MODEL slx_faca82ad9bd2
CONFIG AbsTol = auto
CONFIG EnableMultiTasking = off
CONFIG FixedStep = 1e-3
CONFIG MaxStep = auto
CONFIG MinStep = auto
CONFIG RelTol = 1e-3
CONFIG SampleTimeConstraint = Unconstrained
CONFIG Solver = ode14x
CONFIG SolverName = ode14x
CONFIG StartTime = 0.0
CONFIG StopTime = 15
BLOCK [SubSystem] Classical SMC
  Ports = [1]
  RequestExecContextInheritance = off
BLOCK [Gain] Classical SMC/1//M
  Gain = 1/78020
BLOCK [From] Classical SMC/Actual ouput
  GotoTag = Y
BLOCK [Sum] Classical SMC/Add1
  IconShape = rectangular
  Inputs = -+
  Ports = [2, 1]
BLOCK [Sum] Classical SMC/Add2
  IconShape = rectangular
  Inputs = +++-
  Ports = [4, 1]
BLOCK [Derivative] Classical SMC/Derivative
  NameLocation = left
BLOCK [Derivative] Classical SMC/Derivative1
BLOCK [Derivative] Classical SMC/Derivative2
  NameLocation = top
BLOCK [From] Classical SMC/Disturbance Input
  GotoTag = D
BLOCK [From] Classical SMC/Error
  GotoTag = E
BLOCK [Gain] Classical SMC/Force to Voltage
  Gain = 1/ 2871.14
BLOCK [FromWorkspace] Classical SMC/From Workspace2
  OutDataTypeStr = double
  OutputAfterFinalValue = Setting to zero
  VariableName = Cut1500down
BLOCK [Gain] Classical SMC/Gain, K
  Gain = 0.01
BLOCK [Gain] Classical SMC/Gain1
  Gain = 163
BLOCK [Gain] Classical SMC/Gain2
  Gain = 193.3
BLOCK [Goto] Classical SMC/Goto
  GotoTag = C_SMC
  TagVisibility = global
BLOCK [Goto] Classical SMC/Goto1
  GotoTag = R
BLOCK [Goto] Classical SMC/Goto2
  GotoTag = E
BLOCK [Goto] Classical SMC/Goto3
  GotoTag = Y
BLOCK [Goto] Classical SMC/Goto4
  GotoTag = D
BLOCK [ManualSwitch] Classical SMC/Manual Switch
  CurrentSetting = 0
BLOCK [ManualSwitch] Classical SMC/Manual Switch1
  NameLocation = left
BLOCK [Inport] Classical SMC/Ref
BLOCK [Sin] Classical SMC/Ref. Position, Xref (mm)
  Amplitude = 5
  Frequency = 0.5*(2*pi)
  Offset = 1/2000
  Ports = [0, 1]
  SampleTime = 0
BLOCK [From] Classical SMC/Reference Input
  GotoTag = R
BLOCK [Scope] Classical SMC/Scope
  Floating = off
  NumInputPorts = 1
  Ports = [1]
  ScopeSpecificationString = Simulink.scopes.TimeScopeBlockCfg('CurrentConfiguration', extmgr.ConfigurationSet(extmgr.Configuration('Core','General UI',true),extmgr.Configuration('Core','Source UI',true),extmgr.Configuration('Sources','WiredSimulink',true),extmgr.Configuration('Visuals','Time Domain',true,'SerializedDisplays',{struct('MinYLimReal','-6.29812','MaxYLimReal','6.30846','YLabelReal','','MinYLimMag','0.00000','MaxY...<+1379ch>  <repeated x3 — deduplicated>
BLOCK [Scope] Classical SMC/Scope1
  Floating = off
  NumInputPorts = 4
  Ports = [4]
  ScopeSpecificationString = Simulink.scopes.TimeScopeBlockCfg('CurrentConfiguration', extmgr.ConfigurationSet(extmgr.Configuration('Core','General UI',true),extmgr.Configuration('Core','Source UI',true),extmgr.Configuration('Sources','WiredSimulink',true,'DataLoggingVariableName','ScopeData1'),extmgr.Configuration('Visuals','Time Domain',true,'SerializedDisplays',{struct('MinYLimReal','-0.0201','MaxYLimReal','0.01185','YLabe...<+3440ch>
BLOCK [Signum] Classical SMC/Sgn
BLOCK [Sum] Classical SMC/Sum
  Inputs = |-+
  Ports = [2, 1]
BLOCK [Sum] Classical SMC/Sum1
  Inputs = |-+
  Ports = [2, 1]
BLOCK [Sum] Classical SMC/Sum2
  Inputs = |++
  Ports = [2, 1]
BLOCK [Sum] Classical SMC/Sum3
  Inputs = ++|
  Ports = [2, 1]
BLOCK [TransferFcn] Classical SMC/Transfer Fcn1
  Denominator = [1 163 193.3]
  Numerator = [78020]
BLOCK [TransportDelay] Classical SMC/Transport Delay
  DelayTime = 0.0012
  Ports = [1, 1]
BLOCK [Gain] Classical SMC/lamda, λ
  Gain = lamda
BLOCK [Gain] Classical SMC/lamda1, λ
  Gain = lamda
BLOCK [SubSystem] Disturbance
  Ports = [0, 1]
  RequestExecContextInheritance = off
BLOCK [Outport] Disturbance/D(s)
BLOCK [Gain] Disturbance/Force to Voltage1
  Gain = 1/ 2871.14
BLOCK [FromWorkspace] Disturbance/From Workspace2
  OutDataTypeStr = double
  OutputAfterFinalValue = Setting to zero
  VariableName = Cut1500down
BLOCK [From] From
  GotoTag = C_SMC
  TagVisibility = global
BLOCK [From] From1
  GotoTag = S_SMC
  TagVisibility = global
BLOCK [From] From2
  GotoTag = ST_SMC
  TagVisibility = global
BLOCK [Sin] Ref. Position, Xref (mm)
  Amplitude = 5
  Frequency = 0.5*(2*pi)
  Offset = 1/2000
  Ports = [0, 1]
  SampleTime = 0
BLOCK [SubSystem] ST SMC
  Ports = [1]
  RequestExecContextInheritance = off
BLOCK [Gain] ST SMC/1//M
  Gain = 1/78020
BLOCK [Abs] ST SMC/Abs
  SaturateOnIntegerOverflow = off
BLOCK [From] ST SMC/Actual ouput
  GotoTag = Y
BLOCK [Sum] ST SMC/Add1
  IconShape = rectangular
  Inputs = --+
  Ports = [3, 1]
BLOCK [Sum] ST SMC/Add2
  IconShape = rectangular
  Inputs = +++-
  Ports = [4, 1]
BLOCK [Derivative] ST SMC/Derivative
  NameLocation = left
BLOCK [Derivative] ST SMC/Derivative1
BLOCK [Derivative] ST SMC/Derivative2
  NameLocation = top
BLOCK [From] ST SMC/Disturbance Input
  GotoTag = D
BLOCK [DotProduct] ST SMC/Dot Product
  OutDataTypeStr = Inherit: Inherit via internal rule
BLOCK [From] ST SMC/Error
  GotoTag = E
BLOCK [Gain] ST SMC/Force to Voltage
  Gain = 1/ 2871.14
BLOCK [FromWorkspace] ST SMC/From Workspace2
  OutDataTypeStr = double
  OutputAfterFinalValue = Setting to zero
  VariableName = Cut1500down
BLOCK [Gain] ST SMC/Gain, β
  Gain = 0.08
BLOCK [Gain] ST SMC/Gain1
  Gain = 163
BLOCK [Gain] ST SMC/Gain2
  Gain = 193.3
BLOCK [Goto] ST SMC/Goto
  GotoTag = ST_SMC
  TagVisibility = global
BLOCK [Goto] ST SMC/Goto1
  GotoTag = R
BLOCK [Goto] ST SMC/Goto2
  GotoTag = E
BLOCK [Goto] ST SMC/Goto3
  GotoTag = Y
BLOCK [Goto] ST SMC/Goto4
  GotoTag = D
BLOCK [Integrator] ST SMC/Integrator
  Ports = [1, 1]
BLOCK [ManualSwitch] ST SMC/Manual Switch
  CurrentSetting = 0
BLOCK [ManualSwitch] ST SMC/Manual Switch1
  NameLocation = left
BLOCK [Inport] ST SMC/Ref
BLOCK [Sin] ST SMC/Ref. Position, Xref (mm)
  Amplitude = 5
  Frequency = 0.5*(2*pi)
  Offset = 1/2000
  Ports = [0, 1]
  SampleTime = 0
BLOCK [From] ST SMC/Reference Input
  GotoTag = R
BLOCK [Scope] ST SMC/Scope
  Floating = off
  NumInputPorts = 1
  Ports = [1]
BLOCK [Scope] ST SMC/Scope1
  Floating = off
  NumInputPorts = 4
  Ports = [4]
  ScopeSpecificationString = Simulink.scopes.TimeScopeBlockCfg('CurrentConfiguration', extmgr.ConfigurationSet(extmgr.Configuration('Core','General UI',true),extmgr.Configuration('Core','Source UI',true),extmgr.Configuration('Sources','WiredSimulink',true,'DataLoggingVariableName','ScopeData1'),extmgr.Configuration('Visuals','Time Domain',true,'SerializedDisplays',{struct('MinYLimReal','-0.0201','MaxYLimReal','0.01185','YLabe...<+3440ch>
BLOCK [Signum] ST SMC/Sgn
BLOCK [Sqrt] ST SMC/Sqrt
BLOCK [Sum] ST SMC/Sum
  Inputs = |-+
  Ports = [2, 1]
BLOCK [Sum] ST SMC/Sum1
  Inputs = |-+
  Ports = [2, 1]
BLOCK [Sum] ST SMC/Sum2
  Inputs = |++
  Ports = [2, 1]
BLOCK [Sum] ST SMC/Sum3
  Inputs = ++|
  Ports = [2, 1]
BLOCK [TransferFcn] ST SMC/Transfer Fcn
  Denominator = [1 163 193.3]
  Numerator = [78020]
BLOCK [TransportDelay] ST SMC/Transport Delay
  DelayTime = 0.0012
  Ports = [1, 1]
BLOCK [Gain] ST SMC/alpha, α
  Gain = 0.0024
BLOCK [Gain] ST SMC/lamda, λ
  Gain = lamdast
BLOCK [Gain] ST SMC/lamda1, λ
  Gain = lamdast
BLOCK [Scope] Scope
  Floating = off
  NumInputPorts = 3
  Ports = [3]
  ScopeSpecificationString = Simulink.scopes.TimeScopeBlockCfg('CurrentConfiguration', extmgr.ConfigurationSet(extmgr.Configuration('Core','General UI',true),extmgr.Configuration('Core','Source UI',true),extmgr.Configuration('Sources','WiredSimulink',true,'DataLoggingVariableName','SMC_out','DataLogging',true,'DataLoggingSaveFormat','StructureWithTime'),extmgr.Configuration('Visuals','Time Domain',true,'SerializedDisplays',{s...<+1919ch>
BLOCK [SubSystem] Simoid SMC
  Ports = [1]
  RequestExecContextInheritance = off
BLOCK [Gain] Simoid SMC/1//M
  Gain = 1/78020
BLOCK [Abs] Simoid SMC/Abs
  SaturateOnIntegerOverflow = off
BLOCK [From] Simoid SMC/Actual ouput
  GotoTag = Y
BLOCK [Sum] Simoid SMC/Add1
  IconShape = rectangular
  Inputs = -+
  Ports = [2, 1]
BLOCK [Sum] Simoid SMC/Add2
  IconShape = rectangular
  Inputs = +++-
  Ports = [4, 1]
BLOCK [Derivative] Simoid SMC/Derivative
  NameLocation = left
BLOCK [Derivative] Simoid SMC/Derivative1
BLOCK [Derivative] Simoid SMC/Derivative2
  NameLocation = top
BLOCK [From] Simoid SMC/Disturbance Input
  GotoTag = D
BLOCK [DotProduct] Simoid SMC/Dot Product
  OutDataTypeStr = Inherit: Inherit via internal rule
BLOCK [From] Simoid SMC/Error
  GotoTag = E
BLOCK [Math] Simoid SMC/Exp
  Operator = reciprocal
  Ports = [1, 1]
BLOCK [Gain] Simoid SMC/Force to Voltage
  Gain = 1/ 2871.14
BLOCK [FromWorkspace] Simoid SMC/From Workspace2
  OutDataTypeStr = double
  OutputAfterFinalValue = Setting to zero
  VariableName = Cut1500down
BLOCK [Gain] Simoid SMC/Gain, K
  Gain = 0.1
BLOCK [Gain] Simoid SMC/Gain1
  Gain = 163
BLOCK [Gain] Simoid SMC/Gain2
  Gain = 193.3
BLOCK [Goto] Simoid SMC/Goto
  GotoTag = S_SMC
  TagVisibility = global
BLOCK [Goto] Simoid SMC/Goto1
  GotoTag = R
BLOCK [Goto] Simoid SMC/Goto2
  GotoTag = E
BLOCK [Goto] Simoid SMC/Goto3
  GotoTag = Y
BLOCK [Goto] Simoid SMC/Goto4
  GotoTag = D
BLOCK [ManualSwitch] Simoid SMC/Manual Switch
  CurrentSetting = 0
BLOCK [ManualSwitch] Simoid SMC/Manual Switch1
  NameLocation = left
BLOCK [Inport] Simoid SMC/Ref
BLOCK [Sin] Simoid SMC/Ref. Position, Xref (mm)
  Amplitude = 5
  Frequency = 0.5*(2*pi)
  Offset = 1/2000
  Ports = [0, 1]
  SampleTime = 0
BLOCK [From] Simoid SMC/Reference Input
  GotoTag = R
BLOCK [Scope] Simoid SMC/Scope
  Floating = off
  NumInputPorts = 1
  Ports = [1]
BLOCK [Scope] Simoid SMC/Scope1
  Floating = off
  NumInputPorts = 4
  Ports = [4]
  ScopeSpecificationString = Simulink.scopes.TimeScopeBlockCfg('CurrentConfiguration', extmgr.ConfigurationSet(extmgr.Configuration('Core','General UI',true),extmgr.Configuration('Core','Source UI',true),extmgr.Configuration('Sources','WiredSimulink',true,'DataLoggingVariableName','ScopeData1'),extmgr.Configuration('Visuals','Time Domain',true,'SerializedDisplays',{struct('MinYLimReal','-0.01749','MaxYLimReal','0.01015','YLab...<+3442ch>
BLOCK [Sum] Simoid SMC/Sum
  Inputs = |-+
  Ports = [2, 1]
BLOCK [Sum] Simoid SMC/Sum1
  Inputs = |-+
  Ports = [2, 1]
BLOCK [Sum] Simoid SMC/Sum2
  Inputs = |++
  Ports = [2, 1]
BLOCK [Sum] Simoid SMC/Sum3
  Inputs = ++|
  Ports = [2, 1]
BLOCK [Sum] Simoid SMC/Sum4
  Inputs = |++
  Ports = [2, 1]
BLOCK [TransferFcn] Simoid SMC/Transfer Fcn
  Denominator = [1 163 193.3]
  Numerator = [78020]
BLOCK [TransportDelay] Simoid SMC/Transport Delay
  DelayTime = 0.0012
  Ports = [1, 1]
BLOCK [Constant] Simoid SMC/delta
  Value = 20
BLOCK [Gain] Simoid SMC/lamda, λ
  Gain = lamda
BLOCK [Gain] Simoid SMC/lamda1, λ
  Gain = lamda
BLOCK [Terminator] Terminator
LINE Classical SMC/1//M:1 -> Classical SMC/Add1:2
LINE Classical SMC/Actual ouput:1 -> Classical SMC/Scope1:4
LINE Classical SMC/Add1:1 -> Classical SMC/Sum3:2
LINE Classical SMC/Add2:1 -> Classical SMC/1//M:1
LINE Classical SMC/Derivative1:1 -> Classical SMC/Derivative2:1
LINE Classical SMC/Derivative1:1 -> Classical SMC/Sum1:1
LINE Classical SMC/Derivative2:1 -> Classical SMC/Add2:3
LINE Classical SMC/Derivative:1 -> Classical SMC/Gain1:1
LINE Classical SMC/Derivative:1 -> Classical SMC/Sum1:2
LINE Classical SMC/Disturbance Input:1 -> Classical SMC/Scope1:1
LINE Classical SMC/Error:1 -> Classical SMC/Scope1:2
LINE Classical SMC/Force to Voltage:1 -> Classical SMC/Goto4:1
LINE Classical SMC/Force to Voltage:1 -> Classical SMC/Manual Switch1:1
LINE Classical SMC/From Workspace2:1 -> Classical SMC/Force to Voltage:1
LINE Classical SMC/Gain, K:1 -> Classical SMC/Add1:1
LINE Classical SMC/Gain1:1 -> Classical SMC/Add2:1
LINE Classical SMC/Gain2:1 -> Classical SMC/Add2:2
LINE Classical SMC/Manual Switch1:1 -> Classical SMC/Sum3:1
LINE Classical SMC/Manual Switch:1 -> Classical SMC/Derivative1:1
LINE Classical SMC/Manual Switch:1 -> Classical SMC/Goto1:1
LINE Classical SMC/Manual Switch:1 -> Classical SMC/Sum:1
LINE Classical SMC/Ref. Position, Xref (mm):1 -> Classical SMC/Manual Switch:1
LINE Classical SMC/Ref:1 -> Classical SMC/Manual Switch:2
LINE Classical SMC/Reference Input:1 -> Classical SMC/Scope1:3
LINE Classical SMC/Sgn:1 -> Classical SMC/Gain, K:1
LINE Classical SMC/Sum1:1 -> Classical SMC/Sum2:2
LINE Classical SMC/Sum1:1 -> Classical SMC/lamda1, λ:1
LINE Classical SMC/Sum2:1 -> Classical SMC/Sgn:1
LINE Classical SMC/Sum3:1 -> Classical SMC/Transfer Fcn1:1
LINE Classical SMC/Sum:1 -> Classical SMC/Goto2:1
LINE Classical SMC/Sum:1 -> Classical SMC/Goto:1
LINE Classical SMC/Sum:1 -> Classical SMC/lamda, λ:1
LINE Classical SMC/Transfer Fcn1:1 -> Classical SMC/Transport Delay:1
LINE Classical SMC/Transport Delay:1 -> Classical SMC/Derivative:1
LINE Classical SMC/Transport Delay:1 -> Classical SMC/Gain2:1
LINE Classical SMC/Transport Delay:1 -> Classical SMC/Goto3:1
LINE Classical SMC/Transport Delay:1 -> Classical SMC/Scope:1
LINE Classical SMC/Transport Delay:1 -> Classical SMC/Sum:2
LINE Classical SMC/lamda, λ:1 -> Classical SMC/Sum2:1
LINE Classical SMC/lamda1, λ:1 -> Classical SMC/Add2:4
LINE Disturbance/Force to Voltage1:1 -> Disturbance/D(s):1
LINE Disturbance/From Workspace2:1 -> Disturbance/Force to Voltage1:1
LINE Disturbance:1 -> Terminator:1
LINE From1:1 -> Scope:2
LINE From2:1 -> Scope:3
LINE From:1 -> Scope:1
LINE Ref. Position, Xref (mm):1 -> Classical SMC:1
LINE Ref. Position, Xref (mm):1 -> ST SMC:1
LINE Ref. Position, Xref (mm):1 -> Simoid SMC:1
LINE ST SMC/1//M:1 -> ST SMC/Add1:3
LINE ST SMC/Abs:1 -> ST SMC/Sqrt:1
LINE ST SMC/Actual ouput:1 -> ST SMC/Scope1:4
LINE ST SMC/Add1:1 -> ST SMC/Sum3:2
LINE ST SMC/Add2:1 -> ST SMC/1//M:1
LINE ST SMC/Derivative1:1 -> ST SMC/Derivative2:1
LINE ST SMC/Derivative1:1 -> ST SMC/Sum1:1
LINE ST SMC/Derivative2:1 -> ST SMC/Add2:3
LINE ST SMC/Derivative:1 -> ST SMC/Gain1:1
LINE ST SMC/Derivative:1 -> ST SMC/Sum1:2
LINE ST SMC/Disturbance Input:1 -> ST SMC/Scope1:1
LINE ST SMC/Dot Product:1 -> ST SMC/Add1:1
LINE ST SMC/Error:1 -> ST SMC/Scope1:2
LINE ST SMC/Force to Voltage:1 -> ST SMC/Goto4:1
LINE ST SMC/Force to Voltage:1 -> ST SMC/Manual Switch1:1
LINE ST SMC/From Workspace2:1 -> ST SMC/Force to Voltage:1
LINE ST SMC/Gain, β:1 -> ST SMC/Integrator:1
LINE ST SMC/Gain1:1 -> ST SMC/Add2:1
LINE ST SMC/Gain2:1 -> ST SMC/Add2:2
LINE ST SMC/Integrator:1 -> ST SMC/Add1:2
LINE ST SMC/Manual Switch1:1 -> ST SMC/Sum3:1
LINE ST SMC/Manual Switch:1 -> ST SMC/Derivative1:1
LINE ST SMC/Manual Switch:1 -> ST SMC/Goto1:1
LINE ST SMC/Manual Switch:1 -> ST SMC/Sum:1
LINE ST SMC/Ref. Position, Xref (mm):1 -> ST SMC/Manual Switch:1
LINE ST SMC/Ref:1 -> ST SMC/Manual Switch:2
LINE ST SMC/Reference Input:1 -> ST SMC/Scope1:3
LINE ST SMC/Sgn:1 -> ST SMC/Dot Product:2
LINE ST SMC/Sgn:1 -> ST SMC/Gain, β:1
LINE ST SMC/Sqrt:1 -> ST SMC/alpha, α:1
LINE ST SMC/Sum1:1 -> ST SMC/Sum2:2
LINE ST SMC/Sum1:1 -> ST SMC/lamda1, λ:1
LINE ST SMC/Sum2:1 -> ST SMC/Abs:1
LINE ST SMC/Sum2:1 -> ST SMC/Sgn:1
LINE ST SMC/Sum3:1 -> ST SMC/Transfer Fcn:1
LINE ST SMC/Sum:1 -> ST SMC/Goto2:1
LINE ST SMC/Sum:1 -> ST SMC/Goto:1
LINE ST SMC/Sum:1 -> ST SMC/lamda, λ:1
LINE ST SMC/Transfer Fcn:1 -> ST SMC/Transport Delay:1
LINE ST SMC/Transport Delay:1 -> ST SMC/Derivative:1
LINE ST SMC/Transport Delay:1 -> ST SMC/Gain2:1
LINE ST SMC/Transport Delay:1 -> ST SMC/Goto3:1
LINE ST SMC/Transport Delay:1 -> ST SMC/Scope:1
LINE ST SMC/Transport Delay:1 -> ST SMC/Sum:2
LINE ST SMC/alpha, α:1 -> ST SMC/Dot Product:1
LINE ST SMC/lamda, λ:1 -> ST SMC/Sum2:1
LINE ST SMC/lamda1, λ:1 -> ST SMC/Add2:4
LINE Simoid SMC/1//M:1 -> Simoid SMC/Add1:2
LINE Simoid SMC/Abs:1 -> Simoid SMC/Sum4:1
LINE Simoid SMC/Actual ouput:1 -> Simoid SMC/Scope1:4
LINE Simoid SMC/Add1:1 -> Simoid SMC/Sum3:2
LINE Simoid SMC/Add2:1 -> Simoid SMC/1//M:1
LINE Simoid SMC/Derivative1:1 -> Simoid SMC/Derivative2:1
LINE Simoid SMC/Derivative1:1 -> Simoid SMC/Sum1:1
LINE Simoid SMC/Derivative2:1 -> Simoid SMC/Add2:3
LINE Simoid SMC/Derivative:1 -> Simoid SMC/Gain1:1
LINE Simoid SMC/Derivative:1 -> Simoid SMC/Sum1:2
LINE Simoid SMC/Disturbance Input:1 -> Simoid SMC/Scope1:1
LINE Simoid SMC/Dot Product:1 -> Simoid SMC/Gain, K:1
LINE Simoid SMC/Error:1 -> Simoid SMC/Scope1:2
LINE Simoid SMC/Exp:1 -> Simoid SMC/Dot Product:2
LINE Simoid SMC/Force to Voltage:1 -> Simoid SMC/Goto4:1
LINE Simoid SMC/Force to Voltage:1 -> Simoid SMC/Manual Switch1:1
LINE Simoid SMC/From Workspace2:1 -> Simoid SMC/Force to Voltage:1
LINE Simoid SMC/Gain, K:1 -> Simoid SMC/Add1:1
LINE Simoid SMC/Gain1:1 -> Simoid SMC/Add2:1
LINE Simoid SMC/Gain2:1 -> Simoid SMC/Add2:2
LINE Simoid SMC/Manual Switch1:1 -> Simoid SMC/Sum3:1
LINE Simoid SMC/Manual Switch:1 -> Simoid SMC/Derivative1:1
LINE Simoid SMC/Manual Switch:1 -> Simoid SMC/Goto1:1
LINE Simoid SMC/Manual Switch:1 -> Simoid SMC/Sum:1
LINE Simoid SMC/Ref. Position, Xref (mm):1 -> Simoid SMC/Manual Switch:1
LINE Simoid SMC/Ref:1 -> Simoid SMC/Manual Switch:2
LINE Simoid SMC/Reference Input:1 -> Simoid SMC/Scope1:3
LINE Simoid SMC/Sum1:1 -> Simoid SMC/Sum2:2
LINE Simoid SMC/Sum1:1 -> Simoid SMC/lamda1, λ:1
LINE Simoid SMC/Sum2:1 -> Simoid SMC/Abs:1
LINE Simoid SMC/Sum2:1 -> Simoid SMC/Dot Product:1
LINE Simoid SMC/Sum3:1 -> Simoid SMC/Transfer Fcn:1
LINE Simoid SMC/Sum4:1 -> Simoid SMC/Exp:1
LINE Simoid SMC/Sum:1 -> Simoid SMC/Goto2:1
LINE Simoid SMC/Sum:1 -> Simoid SMC/Goto:1
LINE Simoid SMC/Sum:1 -> Simoid SMC/lamda, λ:1
LINE Simoid SMC/Transfer Fcn:1 -> Simoid SMC/Transport Delay:1
LINE Simoid SMC/Transport Delay:1 -> Simoid SMC/Derivative:1
LINE Simoid SMC/Transport Delay:1 -> Simoid SMC/Gain2:1
LINE Simoid SMC/Transport Delay:1 -> Simoid SMC/Goto3:1
LINE Simoid SMC/Transport Delay:1 -> Simoid SMC/Scope:1
LINE Simoid SMC/Transport Delay:1 -> Simoid SMC/Sum:2
LINE Simoid SMC/delta:1 -> Simoid SMC/Sum4:2
LINE Simoid SMC/lamda, λ:1 -> Simoid SMC/Sum2:1
LINE Simoid SMC/lamda1, λ:1 -> Simoid SMC/Add2:4
